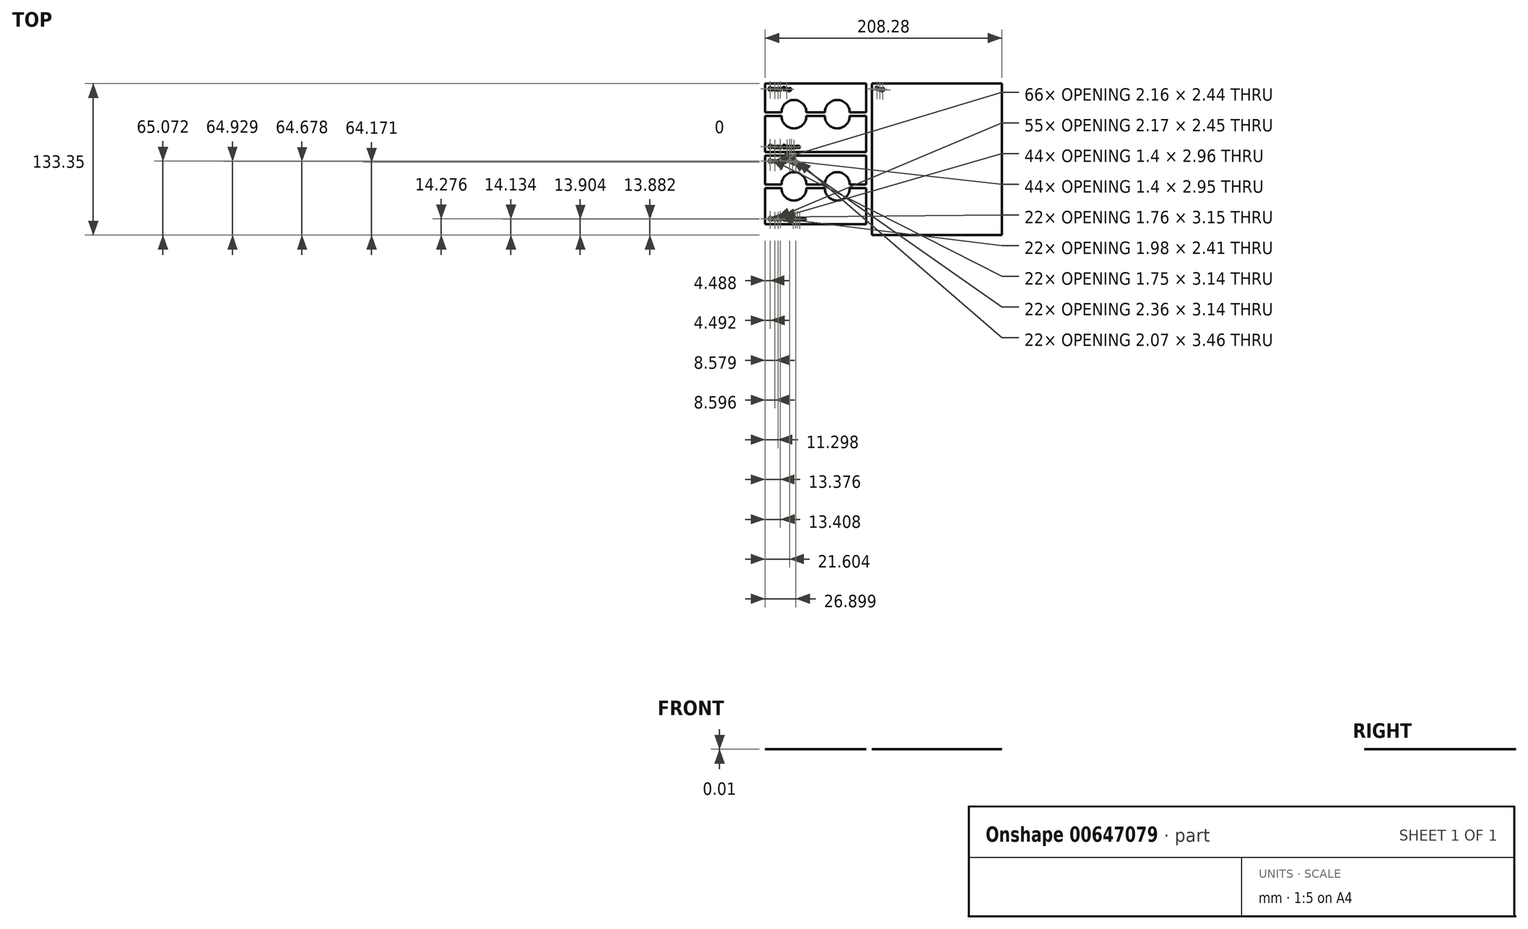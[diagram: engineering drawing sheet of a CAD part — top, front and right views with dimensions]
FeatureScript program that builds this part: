
annotation { "Feature Type Name" : "Feature", "Feature Type Description" : "" }
export const myFeature = defineFeature(function(context is Context, id is Id, definition is map)
    precondition{}
    {
        {
            var Q0;
            Q0=qCreatedBy(makeId("Top.planeOp"),FACE);
            var sketch = newSketch(context, id + "F0", { "sketchPlane" : qUnion([Q0])});
            skLineSegment(sketch, "E0.bottom", {"start": v(-44.45, 0) * mm, "end": v(44.45, 0) * mm});
            skLineSegment(sketch, "E0.top", {"start": v(-44.45, -25.4) * mm, "end": v(-29.97, -25.4) * mm});
            skLineSegment(sketch, "E0.left", {"start": v(-44.45, 0) * mm, "end": v(-44.45, -25.4) * mm});
            skLineSegment(sketch, "E0.right", {"start": v(44.45, 0) * mm, "end": v(44.45, -25.4) * mm});
            skPoint(sketch, "E1", {"position": v(0, 0) * mm});
            skLineSegment(sketch, "E2.bottom", {"start": v(-44.45, -28.58) * mm, "end": v(-29.97, -28.57) * mm});
            skLineSegment(sketch, "E2.top", {"start": v(-44.45, -60.33) * mm, "end": v(44.45, -60.32) * mm});
            skLineSegment(sketch, "E2.left", {"start": v(-44.45, -28.57) * mm, "end": v(-44.45, -60.33) * mm});
            skLineSegment(sketch, "E2.right", {"start": v(44.45, -28.57) * mm, "end": v(44.45, -60.33) * mm});
            skArc(sketch, "E3", {"start": v(-8.13, -25.4) * mm, "mid": v(-19.05, -14.48) * mm, "end": v(-29.97, -25.4) * mm});
            skArc(sketch, "E4", {"start": v(29.97, -25.4) * mm, "mid": v(19.05, -14.48) * mm, "end": v(8.13, -25.4) * mm});
            skArc(sketch, "E5", {"start": v(-29.97, -28.57) * mm, "mid": v(-19.05, -39.5) * mm, "end": v(-8.13, -28.57) * mm});
            skArc(sketch, "E6", {"start": v(8.13, -28.57) * mm, "mid": v(19.05, -39.5) * mm, "end": v(29.97, -28.57) * mm});
            skLineSegment(sketch, "E7.trimOffspring", {"start": v(-8.13, -25.4) * mm, "end": v(8.13, -25.4) * mm});
            skLineSegment(sketch, "E8.trimOffspring", {"start": v(29.97, -25.4) * mm, "end": v(44.45, -25.4) * mm});
            skLineSegment(sketch, "E9.trimOffspring", {"start": v(29.97, -28.57) * mm, "end": v(44.45, -28.57) * mm});
            skLineSegment(sketch, "E10.trimOffspring", {"start": v(-8.13, -28.57) * mm, "end": v(8.13, -28.57) * mm});
            skText(sketch, "E11", { "text": "Front Top", "fontName": "OpenSans-Regular.ttf"});
            skText(sketch, "E12", { "text": "Front Bottom", "fontName": "OpenSans-Regular.ttf"});
            skLineSegment(sketch, "E13.bottom", {"start": v(-44.45, -63.5) * mm, "end": v(44.45, -63.5) * mm});
            skLineSegment(sketch, "E13.top", {"start": v(-44.45, -88.9) * mm, "end": v(-29.97, -88.9) * mm});
            skLineSegment(sketch, "E13.left", {"start": v(-44.45, -63.5) * mm, "end": v(-44.45, -88.9) * mm});
            skLineSegment(sketch, "E13.right", {"start": v(44.45, -63.5) * mm, "end": v(44.45, -88.9) * mm});
            skPoint(sketch, "E14", {"position": v(0, -63.5) * mm});
            skLineSegment(sketch, "E15.bottom", {"start": v(-44.45, -92.08) * mm, "end": v(-29.97, -92.08) * mm});
            skLineSegment(sketch, "E15.top", {"start": v(-44.45, -123.83) * mm, "end": v(44.45, -123.83) * mm});
            skLineSegment(sketch, "E15.left", {"start": v(-44.45, -92.08) * mm, "end": v(-44.45, -123.83) * mm});
            skLineSegment(sketch, "E15.right", {"start": v(44.45, -92.08) * mm, "end": v(44.45, -123.82) * mm});
            skArc(sketch, "E16", {"start": v(-8.13, -88.9) * mm, "mid": v(-19.05, -77.98) * mm, "end": v(-29.97, -88.9) * mm});
            skArc(sketch, "E17", {"start": v(29.97, -88.9) * mm, "mid": v(19.05, -77.98) * mm, "end": v(8.13, -88.9) * mm});
            skArc(sketch, "E18", {"start": v(-29.97, -92.08) * mm, "mid": v(-19.05, -103) * mm, "end": v(-8.13, -92.07) * mm});
            skArc(sketch, "E19", {"start": v(8.13, -92.08) * mm, "mid": v(19.05, -103) * mm, "end": v(29.97, -92.08) * mm});
            skLineSegment(sketch, "E20.trimOffspring", {"start": v(-8.13, -88.9) * mm, "end": v(8.13, -88.9) * mm});
            skLineSegment(sketch, "E21.trimOffspring", {"start": v(29.97, -88.9) * mm, "end": v(44.45, -88.9) * mm});
            skLineSegment(sketch, "E22.trimOffspring", {"start": v(29.97, -92.08) * mm, "end": v(44.45, -92.08) * mm});
            skLineSegment(sketch, "E23.trimOffspring", {"start": v(-8.13, -92.08) * mm, "end": v(8.13, -92.08) * mm});
            skText(sketch, "E24", { "text": "Front -1 Top", "fontName": "OpenSans-Regular.ttf"});
            skText(sketch, "E25", { "text": "Front -1 Bottom", "fontName": "OpenSans-Regular.ttf"});
            skLineSegment(sketch, "E26.bottom", {"start": v(49.53, 0) * mm, "end": v(163.83, 0) * mm});
            skLineSegment(sketch, "E26.top", {"start": v(49.53, -133.35) * mm, "end": v(163.83, -133.35) * mm});
            skLineSegment(sketch, "E26.left", {"start": v(49.53, 0) * mm, "end": v(49.53, -133.35) * mm});
            skLineSegment(sketch, "E26.right", {"start": v(163.83, 0) * mm, "end": v(163.83, -133.35) * mm});
            skText(sketch, "E27", { "text": "Top", "fontName": "OpenSans-Regular.ttf"});
            const initialGuessF0  = {"E11": [-0.04127, -0.00635, 1, 0, 0.00318], "E12": [-0.04127, -0.05715, 1, 0, 0.00317], "E24": [-0.04127, -0.06985, 1, 0, 0.00317], "E25": [-0.04127, -0.12065, 1, 0, 0.00318], "E27": [0.0527, -0.00635, 1, 0, 0.00317]};
            skSetInitialGuess(sketch, initialGuessF0);
            skSolve(sketch);
        }
        {
            var Q0;
            Q0 = qSketchRegion(id + "F0", true);
            extrude(context, id + "F1", {"entities" : qUnion([Q0]), "depth" : 3 / 203.2 * mm, "offsetDistance" : 25.4 * mm});
        }
    });
